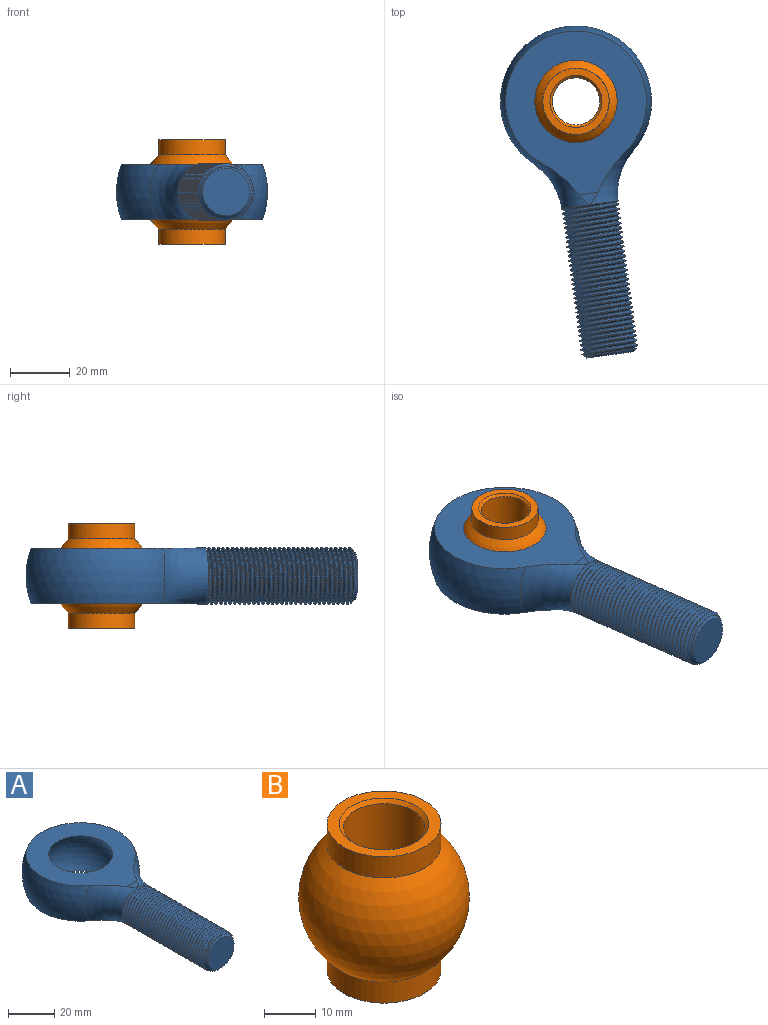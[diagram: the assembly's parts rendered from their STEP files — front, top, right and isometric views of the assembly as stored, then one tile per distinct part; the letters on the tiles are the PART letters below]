
ASSEMBLY  parts=2 mates=1
PART A: 16 faces, bbox 67.3x112.7x67.3 mm
  f0: sphere r=16.67mm, area 1953.6mm2, adj f12,f14
  f1: sphere r=25.4mm, area 2383.1mm2, adj f2,f6,f12,f14
  f2: torus R=30.48mm, axis (0,-1,0), area 417.3mm2, adj f1,f11,f12,f13,f14,f15
  f3: cone r=9.53mm half-angle=45deg, axis (0,1,0), area 72.3mm2, adj f4,f7,f8,f9,f10
  f4: cone r=9.53mm half-angle=45deg, axis (0,1,0), area 8.9mm2, adj f3,f5,f9,f10
  f5: cylinder r=9.53mm len=49.21mm, axis (0,1,0), area 368.2mm2, adj f4,f6,f9,f10
  f6: torus R=30.48mm, axis (0,-1,0), area 417.3mm2, adj f1,f5,f11,f12,f13,f14,f15
  f7: plane 15.88x15.88mm, normal (0,-1,0), area 197.9mm2, adj f3
  f8: bspline ~51x16.99mm, area 335.8mm2, adj f3,f9,f10,f11
  f9: bspline ~51.59x19.05mm, area 2115.3mm2, adj f3,f4,f5,f8,f11
  f10: bspline ~50.84x19.05mm, area 2111.4mm2, adj f3,f4,f5,f8,f11
  f11: plane 19.68x19.68mm, normal (0,-1,0), area 29.6mm2, adj f2,f6,f8,f9,f10
  f12: plane 56.18x48.61mm, normal (0,0,1), area 1256.4mm2, adj f0,f1,f2,f6,f13
  f13: plane 6.99x4.32mm, normal (0,0.05,1), area 13.8mm2, adj f2,f6,f12
  f14: plane 56.18x48.61mm, normal (0,0,-1), area 1257.8mm2, adj f0,f1,f2,f6,f15
  f15: plane 6.99x4.32mm, normal (0,0.05,-1), area 13.7mm2, adj f2,f6,f14
PART B: 8 faces, bbox 33.3x33.3x34.9 mm
  f0: cone r=7.94mm half-angle=45deg, axis (0,0,1), area 58.8mm2, adj f2,f6
  f1: cone r=7.94mm half-angle=45deg, axis (0,0,-1), area 58.8mm2, adj f2,f7
  f2: cylinder r=7.94mm len=33.34mm, axis (0,0,1), area 1662.6mm2, adj f0,f1
  f3: cylinder r=11.11mm len=22.23mm, axis (0,0,-1), area 351.8mm2, adj f5,f7
  f4: cylinder r=11.11mm len=22.23mm, axis (0,0,-1), area 351.8mm2, adj f5,f6
  f5: sphere r=16.67mm, area 2602.4mm2, adj f3,f4
  f6: plane 22.23x22.23mm, normal (0,0,1), area 148.4mm2, adj f0,f4
  f7: plane 22.23x22.23mm, normal (0,0,-1), area 148.4mm2, adj f1,f3
PLACE A rot(axis=(0,0,1),7.7deg) t=(55.76,11.83,27.02)mm
PLACE B t=(51.09,11.52,27.02)mm
MATE ball A.f0 <-> B.f0  axis (0,0,1) through (51.09,46.44,27.02)mm
